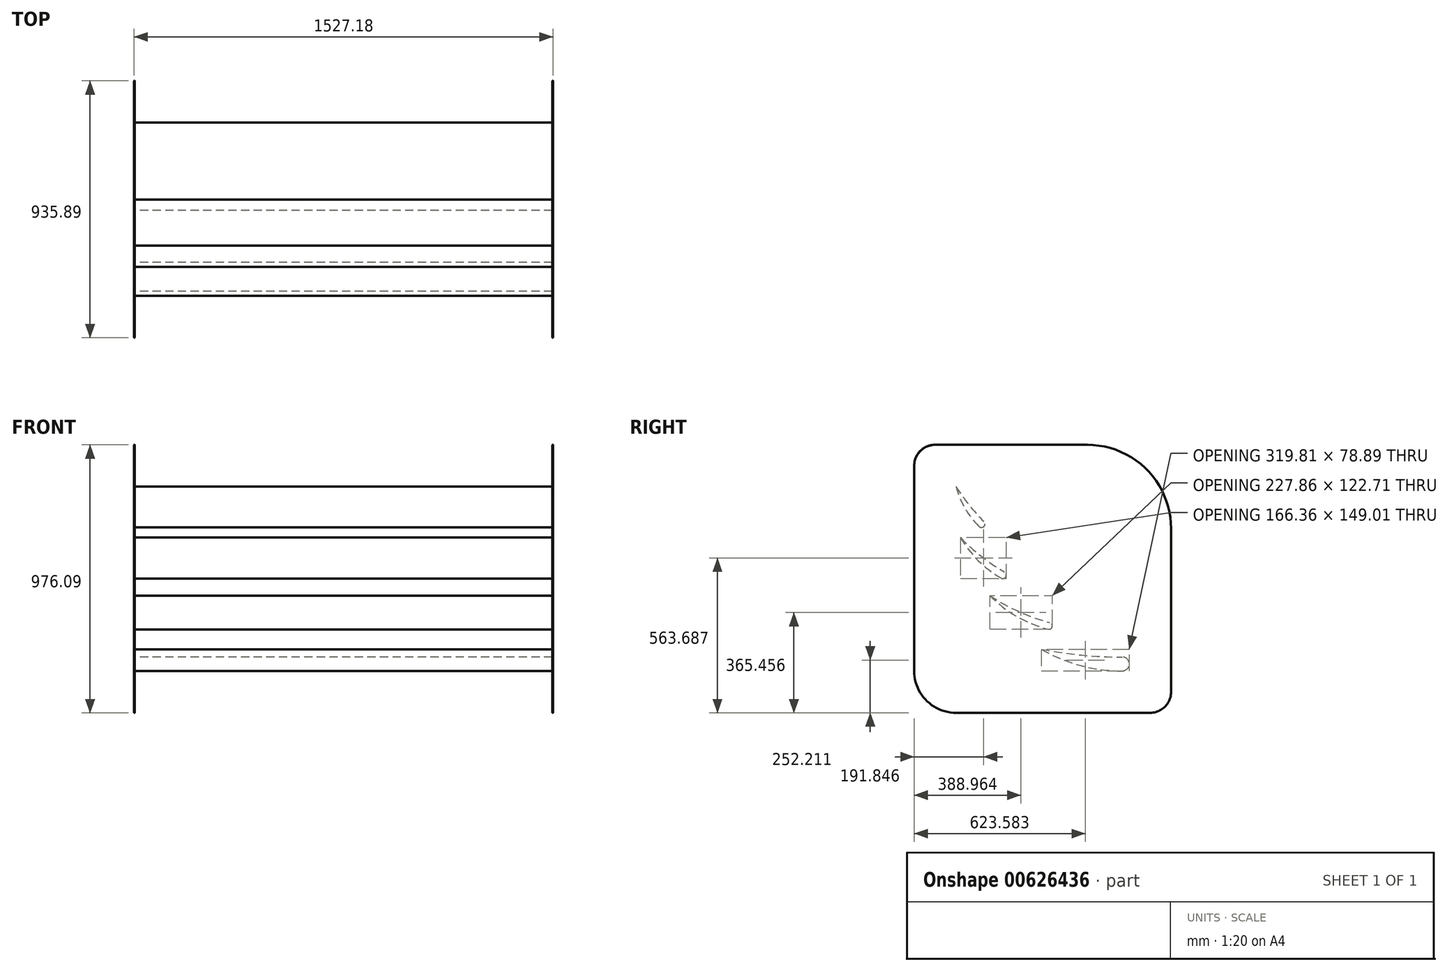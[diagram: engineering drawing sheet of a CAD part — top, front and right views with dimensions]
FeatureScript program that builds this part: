
annotation { "Feature Type Name" : "Feature", "Feature Type Description" : "" }
export const myFeature = defineFeature(function(context is Context, id is Id, definition is map)
    precondition{}
    {
        {
            var Q0;
            Q0=qCreatedBy(makeId("Right.planeOp"),FACE);
            var sketch = newSketch(context, id + "F0", { "sketchPlane" : qUnion([Q0])});
            skArc(sketch, "E0", {"start": v(0, -588.83) * mm, "mid": v(152.4, -568.76) * mm, "end": v(294.41, -509.94) * mm});
            skArc(sketch, "E1", {"start": v(0, -588.83) * mm, "mid": v(-25.4, -563.43) * mm, "end": v(0, -538.03) * mm});
            skArc(sketch, "E2", {"start": v(0, -538.03) * mm, "mid": v(147.88, -531) * mm, "end": v(294.41, -509.94) * mm});
            skSolve(sketch);
        }
        {
            var Q0;
            Q0=makeQuery(id+"F0.imprint","IMPRINT",FACE,{"disambiguationData":[TD([[makeQuery(id+"F0.imprint","IMPRINT",EDGE,{"derivedFrom":sQuery(id+"F0.wireOp",EDGE,"E0")}),1.0]])]});
            extrude(context, id + "F1", {"entities" : qUnion([Q0]), "depth" : 762 * mm, "offsetDistance" : 25.4 * mm});
        }
        {
            var Q0;
            Q0=qCreatedBy(makeId("Right.planeOp"),FACE);
            var sketch = newSketch(context, id + "F2", { "sketchPlane" : qUnion([Q0])});
            skArc(sketch, "E3", {"start": v(271.07, -436.8) * mm, "mid": v(385.12, -389.57) * mm, "end": v(483.06, -314.42) * mm});
            skArc(sketch, "E4", {"start": v(271.07, -436.8) * mm, "mid": v(255.52, -427.83) * mm, "end": v(264.5, -412.27) * mm});
            skArc(sketch, "E5", {"start": v(264.5, -412.27) * mm, "mid": v(377.68, -372.06) * mm, "end": v(483.06, -314.42) * mm});
            skSolve(sketch);
        }
        {
            var Q0;
            Q0=qSketchRegion(id+"F2",true);
            extrude(context, id + "F3", {"entities" : qUnion([Q0]), "depth" : 762 * mm, "offsetDistance" : 25.4 * mm});
        }
        {
            var Q0;
            Q0=qCreatedBy(makeId("Right.planeOp"),FACE);
            var sketch = newSketch(context, id + "F4", { "sketchPlane" : qUnion([Q0])});
            skArc(sketch, "E6", {"start": v(441.64, -250.45) * mm, "mid": v(525.05, -186.45) * mm, "end": v(589.06, -103.04) * mm});
            skArc(sketch, "E7", {"start": v(441.64, -250.45) * mm, "mid": v(424.3, -245.8) * mm, "end": v(428.94, -228.46) * mm});
            skArc(sketch, "E8", {"start": v(428.94, -228.46) * mm, "mid": v(513.42, -171.4) * mm, "end": v(589.06, -103.04) * mm});
            skSolve(sketch);
        }
        {
            var Q0;
            Q0=qSketchRegion(id+"F4",true);
            extrude(context, id + "F5", {"entities" : qUnion([Q0]), "depth" : 762 * mm, "offsetDistance" : 25.4 * mm});
        }
        {
            var Q0;
            Q0=qCreatedBy(makeId("Right.planeOp"),FACE);
            var sketch = newSketch(context, id + "F6", { "sketchPlane" : qUnion([Q0])});
            skArc(sketch, "E9", {"start": v(521.97, -62.55) * mm, "mid": v(573.37, 4.45) * mm, "end": v(605.7, 82.46) * mm});
            skArc(sketch, "E10", {"start": v(521.97, -62.55) * mm, "mid": v(504, -62.55) * mm, "end": v(504, -44.59) * mm});
            skArc(sketch, "E11", {"start": v(504, -44.59) * mm, "mid": v(558.36, 16.13) * mm, "end": v(605.7, 82.46) * mm});
            skSolve(sketch);
        }
        {
            var Q0;
            Q0 = qSketchRegion(id + "F6", true);
            extrude(context, id + "F7", {"entities" : qUnion([Q0]), "depth" : 762 * mm, "offsetDistance" : 25.4 * mm});
        }
        {
            var Q0;
            Q0=makeQuery(id+"F1.opExtrude","CAP_FACE",FACE,{"disambiguationData":[OSD([sQuery(id+"F0.wireOp",EDGE,"E0"),sQuery(id+"F0.wireOp",EDGE,"E1"),sQuery(id+"F0.wireOp",EDGE,"E2")])],"isStart":false});
            var sketch = newSketch(context, id + "F8", { "sketchPlane" : qUnion([Q0])});
            skLineSegment(sketch, "E12.bottom", {"start": v(-177.8, -741.23) * mm, "end": v(758.1, -741.23) * mm});
            skLineSegment(sketch, "E12.top", {"start": v(-177.8, 234.86) * mm, "end": v(758.1, 234.86) * mm});
            skLineSegment(sketch, "E12.left", {"start": v(-177.8, -741.23) * mm, "end": v(-177.8, 234.86) * mm});
            skLineSegment(sketch, "E12.right", {"start": v(758.1, -741.23) * mm, "end": v(758.1, 234.86) * mm});
            skSolve(sketch);
        }
        {
            var Q0;
            Q0=makeQuery(id+"F8.imprint","IMPRINT",FACE,{"disambiguationData":[TD([[makeQuery(id+"F8.imprint","IMPRINT",EDGE,{"derivedFrom":sQuery(id+"F8.wireOp",EDGE,"E12.bottom")}),1.0]])]});
            var Q1;
            Q1=makeQuery(id+"F8.imprint","IMPRINT",FACE,{"disambiguationData":[TD([[makeQuery(id+"F8.imprint","IMPRINT",EDGE,{"derivedFrom":makeQuery(id+"F1.opExtrude","CAP_EDGE",EDGE,{"disambiguationData":[OSD([sQuery(id+"F0.wireOp",EDGE,"E0")])],"isStart":false})}),1.0]])]});
            extrude(context, id + "F9", {"entities" : qUnion([Q0, Q1]), "operationType" : NewBodyOperationType.ADD, "endBound" : BoundingType.SYMMETRIC, "depth" : 3.17 * mm, "offsetDistance" : 25.4 * mm});
        }
        {
            var Q0;
            Q0=makeQuery(id+"F9.opExtrude","SWEPT_EDGE",EDGE,{"disambiguationData":[OSD([sQuery(id+"F8.wireOp",EDGE,"E12.top"),sQuery(id+"F8.wireOp",EDGE,"E12.left")])]});
            fillet(context, id + "F10", {"entities" : qUnion([Q0]), "radius" : 304.8 * mm, "tangentPropagation" : true, "allowEdgeOverflow" : false});
        }
        {
            var Q0;
            Q0=makeQuery(id+"F9.opExtrude","SWEPT_EDGE",EDGE,{"disambiguationData":[OSD([sQuery(id+"F8.wireOp",EDGE,"E12.bottom"),sQuery(id+"F8.wireOp",EDGE,"E12.right")])]});
            fillet(context, id + "F11", {"entities" : qUnion([Q0]), "radius" : 152.4 * mm, "tangentPropagation" : true, "allowEdgeOverflow" : false});
        }
        {
            var Q0;
            Q0=makeQuery(id+"F9.opExtrude","SWEPT_EDGE",EDGE,{"disambiguationData":[OSD([sQuery(id+"F8.wireOp",EDGE,"E12.top"),sQuery(id+"F8.wireOp",EDGE,"E12.right")])]});
            var Q1;
            Q1=makeQuery(id+"F9.opExtrude","SWEPT_EDGE",EDGE,{"disambiguationData":[OSD([sQuery(id+"F8.wireOp",EDGE,"E12.bottom"),sQuery(id+"F8.wireOp",EDGE,"E12.left")])]});
            fillet(context, id + "F12", {"entities" : qUnion([Q0, Q1]), "radius" : 76.2 * mm, "tangentPropagation" : true, "allowEdgeOverflow" : false});
        }
        {
            var Q0;
            {var subQ0=sQuery(id+"F8.wireOp",EDGE,"E12.left");var subQ1=sQuery(id+"F8.wireOp",EDGE,"E12.top");Q0=makeQuery(id+"F10.opFillet","BLEND_EDGE",EDGE,{"blendedFrom":[makeQuery(id+"F9.opExtrude","SWEPT_EDGE",EDGE,{"disambiguationData":[OSD([subQ1,subQ0])]}),makeQuery(id+"F9.opExtrude","CAP_FACE",FACE,{"disambiguationData":[OSD([sQuery(id+"F8.wireOp",EDGE,"E12.bottom"),subQ1,subQ0,sQuery(id+"F8.wireOp",EDGE,"E12.right")])],"isStart":false})],"blendedInto":[makeQuery(id+"F9.opExtrude","CAP_FACE",FACE,{"disambiguationData":[OSD([sQuery(id+"F8.wireOp",EDGE,"E12.bottom"),subQ1,subQ0,sQuery(id+"F8.wireOp",EDGE,"E12.right")])],"isStart":false})]});}
            var Q1;
            {var subQ0=sQuery(id+"F8.wireOp",EDGE,"E12.left");var subQ1=sQuery(id+"F8.wireOp",EDGE,"E12.top");Q1=makeQuery(id+"F10.opFillet","BLEND_EDGE",EDGE,{"blendedFrom":[makeQuery(id+"F9.opExtrude","SWEPT_EDGE",EDGE,{"disambiguationData":[OSD([subQ1,subQ0])]}),makeQuery(id+"F9.opExtrude","CAP_FACE",FACE,{"disambiguationData":[OSD([sQuery(id+"F8.wireOp",EDGE,"E12.bottom"),subQ1,subQ0,sQuery(id+"F8.wireOp",EDGE,"E12.right")])],"isStart":true})],"blendedInto":[makeQuery(id+"F9.opExtrude","CAP_FACE",FACE,{"disambiguationData":[OSD([sQuery(id+"F8.wireOp",EDGE,"E12.bottom"),subQ1,subQ0,sQuery(id+"F8.wireOp",EDGE,"E12.right")])],"isStart":true})]});}
            var Q2;
            {var subQ0=sQuery(id+"F8.wireOp",EDGE,"E12.right");var subQ1=sQuery(id+"F8.wireOp",EDGE,"E12.bottom");Q2=makeQuery(id+"F11.opFillet","BLEND_EDGE",EDGE,{"blendedFrom":[makeQuery(id+"F9.opExtrude","SWEPT_EDGE",EDGE,{"disambiguationData":[OSD([subQ1,subQ0])]}),makeQuery(id+"F9.opExtrude","CAP_FACE",FACE,{"disambiguationData":[OSD([subQ1,sQuery(id+"F8.wireOp",EDGE,"E12.top"),sQuery(id+"F8.wireOp",EDGE,"E12.left"),subQ0])],"isStart":false})],"blendedInto":[makeQuery(id+"F9.opExtrude","CAP_FACE",FACE,{"disambiguationData":[OSD([subQ1,sQuery(id+"F8.wireOp",EDGE,"E12.top"),sQuery(id+"F8.wireOp",EDGE,"E12.left"),subQ0])],"isStart":false})]});}
            var Q3;
            {var subQ0=sQuery(id+"F8.wireOp",EDGE,"E12.right");var subQ1=sQuery(id+"F8.wireOp",EDGE,"E12.bottom");Q3=makeQuery(id+"F11.opFillet","BLEND_EDGE",EDGE,{"blendedFrom":[makeQuery(id+"F9.opExtrude","SWEPT_EDGE",EDGE,{"disambiguationData":[OSD([subQ1,subQ0])]}),makeQuery(id+"F9.opExtrude","CAP_FACE",FACE,{"disambiguationData":[OSD([subQ1,sQuery(id+"F8.wireOp",EDGE,"E12.top"),sQuery(id+"F8.wireOp",EDGE,"E12.left"),subQ0])],"isStart":true})],"blendedInto":[makeQuery(id+"F9.opExtrude","CAP_FACE",FACE,{"disambiguationData":[OSD([subQ1,sQuery(id+"F8.wireOp",EDGE,"E12.top"),sQuery(id+"F8.wireOp",EDGE,"E12.left"),subQ0])],"isStart":true})]});}
            var Q4;
            Q4=makeQuery(id+"F9.opExtrude","CAP_EDGE",EDGE,{"disambiguationData":[OSD([sQuery(id+"F8.wireOp",EDGE,"E12.left")])],"isStart":false});
            var Q5;
            Q5=makeQuery(id+"F9.opExtrude","CAP_EDGE",EDGE,{"disambiguationData":[OSD([sQuery(id+"F8.wireOp",EDGE,"E12.left")])],"isStart":true});
            var Q6;
            {var subQ0=sQuery(id+"F8.wireOp",EDGE,"E12.left");var subQ1=sQuery(id+"F8.wireOp",EDGE,"E12.bottom");Q6=makeQuery(id+"F12.opFillet","BLEND_EDGE",EDGE,{"blendedFrom":[makeQuery(id+"F9.opExtrude","SWEPT_EDGE",EDGE,{"disambiguationData":[OSD([subQ1,subQ0])]}),makeQuery(id+"F9.opExtrude","CAP_FACE",FACE,{"disambiguationData":[OSD([subQ1,sQuery(id+"F8.wireOp",EDGE,"E12.top"),subQ0,sQuery(id+"F8.wireOp",EDGE,"E12.right")])],"isStart":true})],"blendedInto":[makeQuery(id+"F9.opExtrude","CAP_FACE",FACE,{"disambiguationData":[OSD([subQ1,sQuery(id+"F8.wireOp",EDGE,"E12.top"),subQ0,sQuery(id+"F8.wireOp",EDGE,"E12.right")])],"isStart":true})]});}
            var Q7;
            {var subQ0=sQuery(id+"F8.wireOp",EDGE,"E12.left");var subQ1=sQuery(id+"F8.wireOp",EDGE,"E12.bottom");Q7=makeQuery(id+"F12.opFillet","BLEND_EDGE",EDGE,{"blendedFrom":[makeQuery(id+"F9.opExtrude","SWEPT_EDGE",EDGE,{"disambiguationData":[OSD([subQ1,subQ0])]}),makeQuery(id+"F9.opExtrude","CAP_FACE",FACE,{"disambiguationData":[OSD([subQ1,sQuery(id+"F8.wireOp",EDGE,"E12.top"),subQ0,sQuery(id+"F8.wireOp",EDGE,"E12.right")])],"isStart":false})],"blendedInto":[makeQuery(id+"F9.opExtrude","CAP_FACE",FACE,{"disambiguationData":[OSD([subQ1,sQuery(id+"F8.wireOp",EDGE,"E12.top"),subQ0,sQuery(id+"F8.wireOp",EDGE,"E12.right")])],"isStart":false})]});}
            var Q8;
            Q8=makeQuery(id+"F9.opExtrude","CAP_EDGE",EDGE,{"disambiguationData":[OSD([sQuery(id+"F8.wireOp",EDGE,"E12.bottom")])],"isStart":false});
            var Q9;
            Q9=makeQuery(id+"F9.opExtrude","CAP_EDGE",EDGE,{"disambiguationData":[OSD([sQuery(id+"F8.wireOp",EDGE,"E12.bottom")])],"isStart":true});
            var Q10;
            Q10=makeQuery(id+"F9.opExtrude","CAP_EDGE",EDGE,{"disambiguationData":[OSD([sQuery(id+"F8.wireOp",EDGE,"E12.right")])],"isStart":false});
            var Q11;
            Q11=makeQuery(id+"F9.opExtrude","CAP_EDGE",EDGE,{"disambiguationData":[OSD([sQuery(id+"F8.wireOp",EDGE,"E12.right")])],"isStart":true});
            var Q12;
            {var subQ0=sQuery(id+"F8.wireOp",EDGE,"E12.right");var subQ1=sQuery(id+"F8.wireOp",EDGE,"E12.top");Q12=makeQuery(id+"F12.opFillet","BLEND_EDGE",EDGE,{"blendedFrom":[makeQuery(id+"F9.opExtrude","SWEPT_EDGE",EDGE,{"disambiguationData":[OSD([subQ1,subQ0])]}),makeQuery(id+"F9.opExtrude","CAP_FACE",FACE,{"disambiguationData":[OSD([sQuery(id+"F8.wireOp",EDGE,"E12.bottom"),subQ1,sQuery(id+"F8.wireOp",EDGE,"E12.left"),subQ0])],"isStart":false})],"blendedInto":[makeQuery(id+"F9.opExtrude","CAP_FACE",FACE,{"disambiguationData":[OSD([sQuery(id+"F8.wireOp",EDGE,"E12.bottom"),subQ1,sQuery(id+"F8.wireOp",EDGE,"E12.left"),subQ0])],"isStart":false})]});}
            var Q13;
            {var subQ0=sQuery(id+"F8.wireOp",EDGE,"E12.right");var subQ1=sQuery(id+"F8.wireOp",EDGE,"E12.top");Q13=makeQuery(id+"F12.opFillet","BLEND_EDGE",EDGE,{"blendedFrom":[makeQuery(id+"F9.opExtrude","SWEPT_EDGE",EDGE,{"disambiguationData":[OSD([subQ1,subQ0])]}),makeQuery(id+"F9.opExtrude","CAP_FACE",FACE,{"disambiguationData":[OSD([sQuery(id+"F8.wireOp",EDGE,"E12.bottom"),subQ1,sQuery(id+"F8.wireOp",EDGE,"E12.left"),subQ0])],"isStart":true})],"blendedInto":[makeQuery(id+"F9.opExtrude","CAP_FACE",FACE,{"disambiguationData":[OSD([sQuery(id+"F8.wireOp",EDGE,"E12.bottom"),subQ1,sQuery(id+"F8.wireOp",EDGE,"E12.left"),subQ0])],"isStart":true})]});}
            var Q14;
            Q14=makeQuery(id+"F9.opExtrude","CAP_EDGE",EDGE,{"disambiguationData":[OSD([sQuery(id+"F8.wireOp",EDGE,"E12.top")])],"isStart":false});
            var Q15;
            Q15=makeQuery(id+"F9.opExtrude","CAP_EDGE",EDGE,{"disambiguationData":[OSD([sQuery(id+"F8.wireOp",EDGE,"E12.top")])],"isStart":true});
            fillet(context, id + "F13", {"entities" : qUnion([Q0, Q1, Q2, Q3, Q4, Q5, Q6, Q7, Q8, Q9, Q10, Q11, Q12, Q13, Q14, Q15]), "radius" : 1.59 * mm, "tangentPropagation" : true, "allowEdgeOverflow" : false});
        }
        {
            var Q0;
            Q0=makeQuery(id+"F1.opExtrude","SWEPT_BODY",BODY,{"disambiguationData":[OSD([sQuery(id+"F0.wireOp",EDGE,"E0"),sQuery(id+"F0.wireOp",EDGE,"E1"),sQuery(id+"F0.wireOp",EDGE,"E2")])]});
            var Q1;
            Q1=qCreatedBy(makeId("Front.planeOp"),FACE);
            mirror(context, id + "F14", {"entities" : qUnion([Q0]), "mirrorPlane" : qUnion([Q1])});
        }
        {
            var Q0;
            Q0=makeQuery(id+"F1.opExtrude","SWEPT_BODY",BODY,{"disambiguationData":[OSD([sQuery(id+"F0.wireOp",EDGE,"E0"),sQuery(id+"F0.wireOp",EDGE,"E1"),sQuery(id+"F0.wireOp",EDGE,"E2")])]});
            deleteBodies(context, id + "F15", {"entities" : qUnion([Q0])});
        }
        {
            var Q0;
            Q0=makeQuery(id+"F14.opPattern","COPY",BODY,{"derivedFrom":makeQuery(id+"F1.opExtrude","SWEPT_BODY",BODY,{"disambiguationData":[OSD([sQuery(id+"F0.wireOp",EDGE,"E0"),sQuery(id+"F0.wireOp",EDGE,"E1"),sQuery(id+"F0.wireOp",EDGE,"E2")])]}),"instanceName":"1"});
            var Q1;
            Q1=makeQuery(id+"F14.opPattern","COPY",FACE,{"derivedFrom":makeQuery(id+"F1.opExtrude","CAP_FACE",FACE,{"disambiguationData":[OSD([sQuery(id+"F0.wireOp",EDGE,"E0"),sQuery(id+"F0.wireOp",EDGE,"E1"),sQuery(id+"F0.wireOp",EDGE,"E2")])],"isStart":true}),"instanceName":"1"});
            mirror(context, id + "F16", {"operationType" : NewBodyOperationType.ADD, "entities" : qUnion([Q0]), "mirrorPlane" : qUnion([Q1])});
        }
    });
